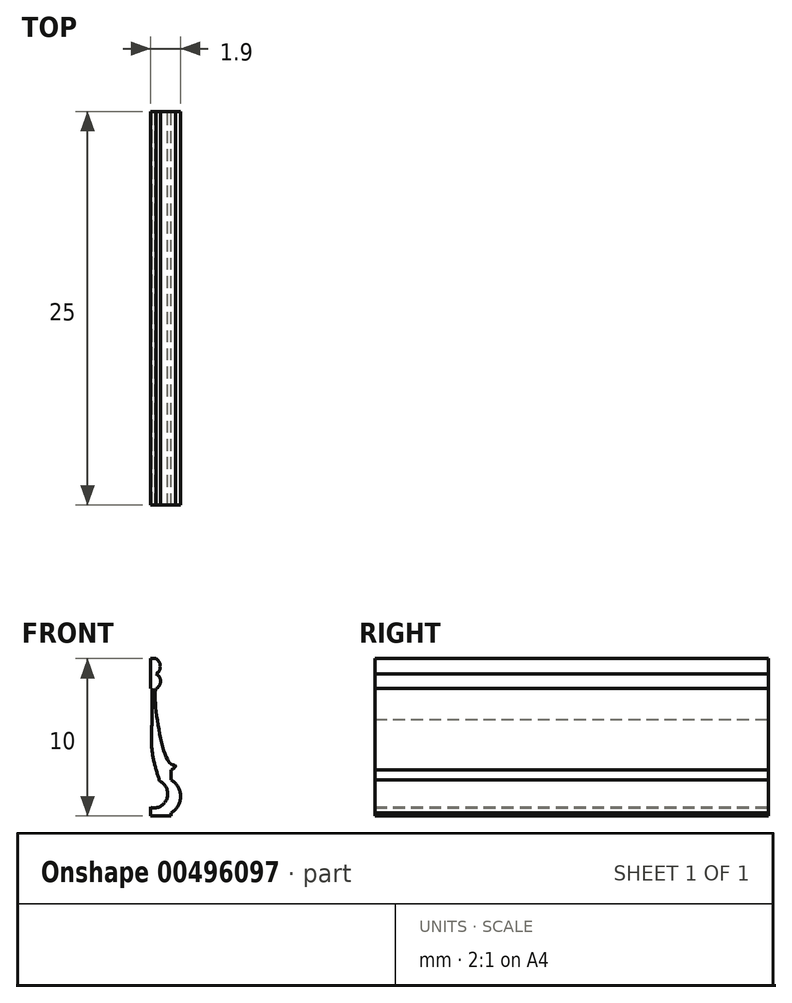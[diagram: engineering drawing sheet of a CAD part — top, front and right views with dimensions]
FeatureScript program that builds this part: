
annotation { "Feature Type Name" : "Feature", "Feature Type Description" : "" }
export const myFeature = defineFeature(function(context is Context, id is Id, definition is map)
    precondition{}
    {
        {
            var Q0;
            Q0=qCreatedBy(makeId("Front.planeOp"),FACE);
            var sketch = newSketch(context, id + "F0", { "sketchPlane" : qUnion([Q0])});
            skLineSegment(sketch, "E0", {"start": v(0, 0) * mm, "end": v(0, -2.7) * mm});
            skLineSegment(sketch, "E1", {"start": v(0, -5) * mm, "end": v(-1.3, -5) * mm});
            skLineSegment(sketch, "E2", {"start": v(-1.3, 3.1) * mm, "end": v(-1.3, 5) * mm});
            skLineSegment(sketch, "E3", {"start": v(-0.97, 5) * mm, "end": v(-1.3, 5) * mm});
            skLineSegment(sketch, "E4", {"start": v(0, -5) * mm, "end": v(0, -4.8) * mm});
            skPoint(sketch, "E5.endSnap0", {"position": v(0, -2.5) * mm});
            skArc(sketch, "E6", {"start": v(0, -4.8) * mm, "mid": v(0.6, -3.75) * mm, "end": v(0, -2.7) * mm});
            skLineSegment(sketch, "E7.trimOffspring", {"start": v(0, -4.8) * mm, "end": v(0, -5) * mm});
            skFitSpline(sketch, "E8", {"points": [v(0, -2.5) * mm, v(-0.2, -2.35) * mm, v(-0.25, -2.21) * mm, v(0.17, -1.98) * mm, v(0.27, -1.8) * mm, v(-0.12, -1.6) * mm, v(-0.97, 3.09) * mm, v(-0.8, 3.11) * mm], "startDerivative": vector(-2.25, 1.5) * mm, "endDerivative": vector(2.42, -1.05) * mm});
            skPoint(sketch, "E9.end.orphan", {"position": v(0, 3.1) * mm});
            skLineSegment(sketch, "E10", {"start": v(-1.2, 3.1) * mm, "end": v(-1.3, 3.1) * mm});
            skLineSegment(sketch, "E11", {"start": v(-1.2, -4.48) * mm, "end": v(-1.3, -4.43) * mm});
            skArc(sketch, "E12", {"start": v(-0.96, 4.02) * mm, "mid": v(-0.68, 4.5) * mm, "end": v(-0.97, 5) * mm});
            skArc(sketch, "E13", {"start": v(-0.96, 3.1) * mm, "mid": v(-0.66, 3.56) * mm, "end": v(-0.96, 4.02) * mm});
            skLineSegment(sketch, "E14", {"start": v(-1.3, -4.43) * mm, "end": v(-1.3, -5) * mm});
            skArc(sketch, "E15", {"start": v(-1.2, -4.48) * mm, "mid": v(-0.24, -3.83) * mm, "end": v(-0.72, -2.78) * mm});
            skFitSpline(sketch, "E16", {"points": [v(-0.72, -2.78) * mm, v(-1.2, -0.9) * mm, v(-1.2, 1.15) * mm], "startDerivative": vector(-1.2, 3.77) * mm, "endDerivative": vector(0.25, 4.1) * mm});
            skPoint(sketch, "E17.orphan", {"position": v(-1.2, -2.7) * mm});
            skLineSegment(sketch, "E18.trimOffspring", {"start": v(-1.2, -0.9) * mm, "end": v(-1.2, 3.1) * mm});
            skArc(sketch, "E19.filletArc", {"start": v(-0.72, -2.78) * mm, "mid": v(-0.72, -2.78) * mm, "end": v(-0.72, -2.78) * mm});
            skPoint(sketch, "E20.visualSharp", {"position": v(-1.2, -4.48) * mm});
            skArc(sketch, "E20.filletArc", {"start": v(-1.2, -4.48) * mm, "mid": v(-1.2, -4.48) * mm, "end": v(-1.2, -4.48) * mm});
            skSolve(sketch);
        }
        {
            var Q0;
            Q0 = qSketchRegion(id + "F0", true);
            extrude(context, id + "F1", {"entities" : qUnion([Q0]), "depth" : 25 * mm});
        }
    });
